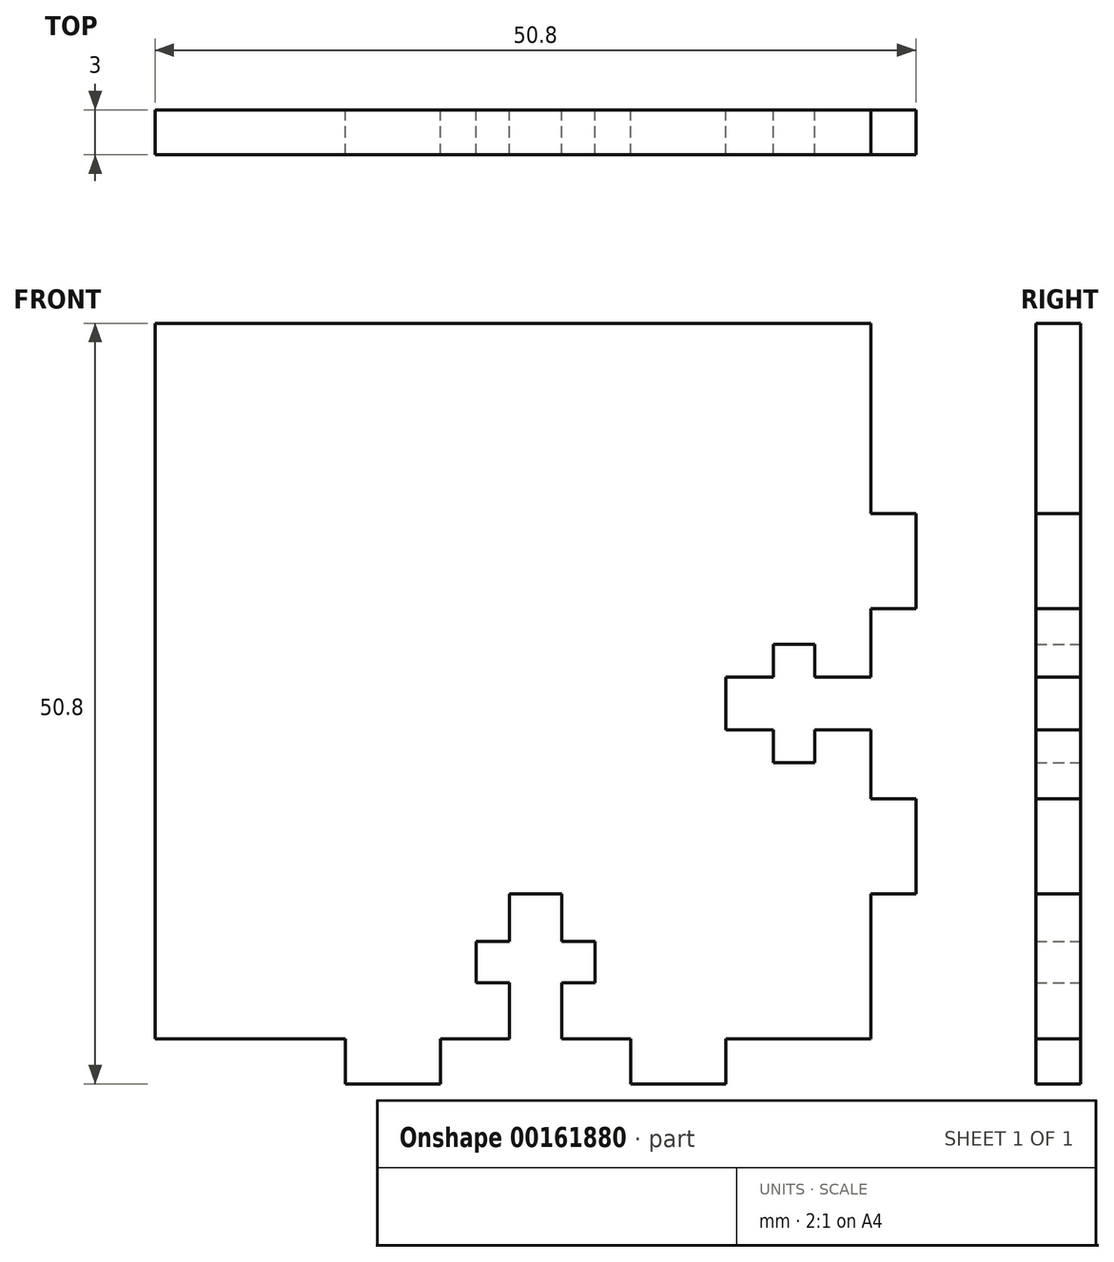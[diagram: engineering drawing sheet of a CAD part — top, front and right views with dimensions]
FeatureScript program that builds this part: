
annotation { "Feature Type Name" : "Feature", "Feature Type Description" : "" }
export const myFeature = defineFeature(function(context is Context, id is Id, definition is map)
    precondition{}
    {
        {
            var Q0;
            Q0=qCreatedBy(makeId("Front.planeOp"),FACE);
            var sketch = newSketch(context, id + "F0", { "sketchPlane" : qUnion([Q0])});
            skLineSegment(sketch, "E0.bottom", {"start": v(-25.4, 25.4) * mm, "end": v(22.4, 25.4) * mm});
            skLineSegment(sketch, "E0.top", {"start": v(-12.7, -25.4) * mm, "end": v(-6.35, -25.4) * mm});
            skLineSegment(sketch, "E0.left", {"start": v(-25.4, 25.4) * mm, "end": v(-25.4, -22.4) * mm});
            skLineSegment(sketch, "E0.right", {"start": v(25.4, 12.7) * mm, "end": v(25.4, 6.35) * mm});
            skPoint(sketch, "E0.middle", {"position": v(0, 0) * mm});
            skLineSegment(sketch, "E1.0", {"start": v(-25.4, -22.4) * mm, "end": v(-12.7, -22.4) * mm});
            skLineSegment(sketch, "E2", {"start": v(-6.35, -22.4) * mm, "end": v(-6.35, -25.4) * mm});
            skLineSegment(sketch, "E3", {"start": v(6.35, -22.4) * mm, "end": v(6.35, -25.4) * mm});
            skLineSegment(sketch, "E4.trimOffspring", {"start": v(6.35, -25.4) * mm, "end": v(12.7, -25.4) * mm});
            skLineSegment(sketch, "E5", {"start": v(-12.7, -22.4) * mm, "end": v(-12.7, -25.4) * mm});
            skLineSegment(sketch, "E6", {"start": v(12.7, -22.4) * mm, "end": v(12.7, -25.4) * mm});
            skLineSegment(sketch, "E7.trimOffspring", {"start": v(-6.35, -22.4) * mm, "end": v(-1.75, -22.4) * mm});
            skLineSegment(sketch, "E8.trimOffspring", {"start": v(12.7, -22.4) * mm, "end": v(22.4, -22.4) * mm});
            skLineSegment(sketch, "E9.0", {"start": v(-1.75, -12.7) * mm, "end": v(1.75, -12.7) * mm});
            skLineSegment(sketch, "E10", {"start": v(-1.75, -12.7) * mm, "end": v(-1.75, -15.87) * mm});
            skLineSegment(sketch, "E11", {"start": v(1.75, -12.7) * mm, "end": v(1.75, -15.87) * mm});
            skLineSegment(sketch, "E12.0", {"start": v(-3.97, -15.87) * mm, "end": v(-1.75, -15.87) * mm});
            skLineSegment(sketch, "E13.0", {"start": v(-3.97, -18.65) * mm, "end": v(-1.75, -18.65) * mm});
            skLineSegment(sketch, "E14", {"start": v(3.97, -15.87) * mm, "end": v(3.97, -18.65) * mm});
            skLineSegment(sketch, "E15.trimOffspring", {"start": v(1.75, -15.87) * mm, "end": v(3.97, -15.87) * mm});
            skLineSegment(sketch, "E16.trimOffspring", {"start": v(1.75, -18.65) * mm, "end": v(3.97, -18.65) * mm});
            skLineSegment(sketch, "E17.trimOffspring", {"start": v(-1.75, -18.65) * mm, "end": v(-1.75, -22.4) * mm});
            skLineSegment(sketch, "E18.trimOffspring", {"start": v(1.75, -18.65) * mm, "end": v(1.75, -22.4) * mm});
            skLineSegment(sketch, "E19.trimOffspring", {"start": v(1.75, -22.4) * mm, "end": v(6.35, -22.4) * mm});
            skLineSegment(sketch, "E20", {"start": v(-3.97, -15.87) * mm, "end": v(-3.97, -18.65) * mm});
            skLineSegment(sketch, "E21", {"start": v(22.4, -6.35) * mm, "end": v(25.4, -6.35) * mm});
            skLineSegment(sketch, "E22", {"start": v(22.4, 6.35) * mm, "end": v(25.4, 6.35) * mm});
            skLineSegment(sketch, "E23.trimOffspring", {"start": v(22.4, -6.35) * mm, "end": v(22.4, -1.75) * mm});
            skLineSegment(sketch, "E24.0", {"start": v(12.7, -1.75) * mm, "end": v(12.7, 1.75) * mm});
            skLineSegment(sketch, "E25", {"start": v(12.7, -1.75) * mm, "end": v(15.87, -1.75) * mm});
            skLineSegment(sketch, "E26", {"start": v(12.7, 1.75) * mm, "end": v(15.87, 1.75) * mm});
            skLineSegment(sketch, "E27.0", {"start": v(15.87, -3.96) * mm, "end": v(15.87, -1.75) * mm});
            skLineSegment(sketch, "E28.0", {"start": v(18.65, -3.96) * mm, "end": v(18.65, -1.75) * mm});
            skLineSegment(sketch, "E29", {"start": v(15.87, 3.96) * mm, "end": v(18.65, 3.96) * mm});
            skLineSegment(sketch, "E30.trimOffspring", {"start": v(15.87, 1.75) * mm, "end": v(15.87, 3.96) * mm});
            skLineSegment(sketch, "E31.trimOffspring", {"start": v(18.65, 1.75) * mm, "end": v(18.65, 3.96) * mm});
            skLineSegment(sketch, "E32.trimOffspring", {"start": v(18.65, -1.75) * mm, "end": v(22.4, -1.75) * mm});
            skLineSegment(sketch, "E33.trimOffspring", {"start": v(18.65, 1.75) * mm, "end": v(22.4, 1.75) * mm});
            skLineSegment(sketch, "E34.trimOffspring", {"start": v(22.4, 1.75) * mm, "end": v(22.4, 6.35) * mm});
            skLineSegment(sketch, "E35", {"start": v(15.87, -3.96) * mm, "end": v(18.65, -3.96) * mm});
            skLineSegment(sketch, "E36", {"start": v(12.7, 0) * mm, "end": v(25.4, 0) * mm, "construction": true});
            skLineSegment(sketch, "E37.trimOffspring", {"start": v(25.4, -6.35) * mm, "end": v(25.4, -12.7) * mm});
            skLineSegment(sketch, "E38", {"start": v(22.4, -12.7) * mm, "end": v(25.4, -12.7) * mm});
            skLineSegment(sketch, "E39", {"start": v(22.4, -12.7) * mm, "end": v(22.4, -22.4) * mm});
            skLineSegment(sketch, "E40", {"start": v(25.4, 12.7) * mm, "end": v(22.4, 12.7) * mm});
            skLineSegment(sketch, "E41", {"start": v(22.4, 12.7) * mm, "end": v(22.4, 25.4) * mm});
            skPoint(sketch, "E42.orphan", {"position": v(25.4, 25.4) * mm});
            skSolve(sketch);
        }
        {
            var Q0;
            Q0 = qSketchRegion(id + "F0", true);
            extrude(context, id + "F1", {"entities" : qUnion([Q0]), "depth" : 3 * mm});
        }
    });
